# Revit family: X-157CP
name_source: partatom
category: Plumbing Fixtures
revit_build: Autodesk Revit Architecture 2012 (Build: 20110309_2315(x64)
units: mm (PartAtom-declared; Revit-internal decimal feet)

## types (1)
- X-157CP
    Aerator = C-M22X1-FLEX
    Assembly Code = D2010
    Basin outlet = 066TU140
    CW Connection = Yes
    CWFU = 0
    Cost = 0 $
    Default Elevation = 0' - 0"
    Description = Three hole with centre outlet. 1/2"BSP male inlets
    HW Connection = Yes
    HWFU = 0
    Headpart clockwise closing = S-21-1CLOCK
    Headpart complete = P-21-3X
    Keynote = 2 x 350mm spout flexible conections for wide range of centre distances
    Manufacturer = COBRA
    Material = Chrome - poluished
    Model = X-157CP
    Range = Ixion
    Side body to spout connection hoses = C-15/350
    Sidevalves = X-21/522
    Type Comments = SANS 226 TYPE 2
    URL = http://www.cobra.co.za
    Vent Connection = No
    WFU = 0
    Waste Connection = No

## geometry (parser evidence)
native form markers: Blend x3
no freeform markers — native parametric forms only
